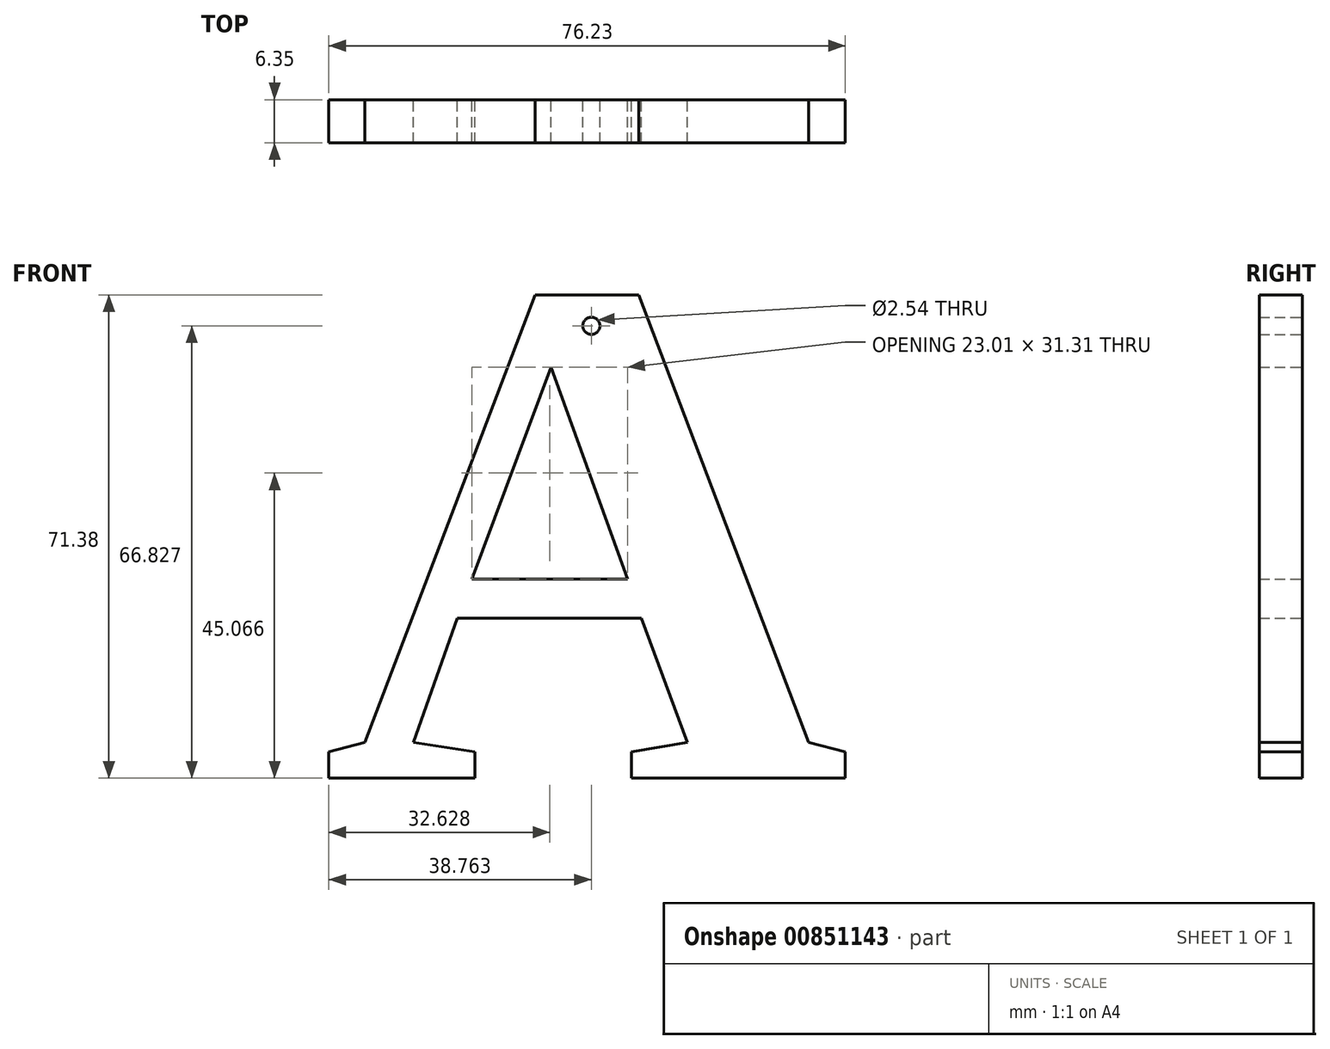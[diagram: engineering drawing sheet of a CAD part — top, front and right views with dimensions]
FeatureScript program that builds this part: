
annotation { "Feature Type Name" : "Feature", "Feature Type Description" : "" }
export const myFeature = defineFeature(function(context is Context, id is Id, definition is map)
    precondition{}
    {
        {
            var Q0;
            Q0=qCreatedBy(makeId("Front.planeOp"),FACE);
            var sketch = newSketch(context, id + "F0", { "sketchPlane" : qUnion([Q0])});
            skText(sketch, "E0", { "text": "A", "fontName": "Tinos-Bold.ttf"});
            const initialGuessF0  = {"E0": [-0.0566, -0.03993, 1, 0, 0.07785]};
            skSetInitialGuess(sketch, initialGuessF0);
            skSolve(sketch);
        }
        {
            var Q0;
            Q0=makeQuery(id+"F0.imprint","IMPRINT",FACE,{"disambiguationData":[TD([[makeQuery(id+"F0.imprint","IMPRINT",EDGE,{"derivedFrom":sQuery(id+"F0.wireOp",EDGE,"E0.sketch_text.stroke-0")}),-1.0]])]});
            var sketch = newSketch(context, id + "F1", { "sketchPlane" : qUnion([Q0])});
            skPoint(sketch, "E1", {"position": v(-16.78, 26.9) * mm});
            skSolve(sketch);
        }
        {
            var Q0;
            Q0=makeQuery(id+"F0.imprint","IMPRINT",FACE,{"disambiguationData":[TD([[makeQuery(id+"F0.imprint","IMPRINT",EDGE,{"derivedFrom":sQuery(id+"F0.wireOp",EDGE,"E0.sketch_text.stroke-0")}),-1.0]])]});
            extrude(context, id + "F2", {"entities" : qUnion([Q0]), "depth" : 6.35 * mm, "offsetDistance" : 25.4 * mm});
        }
        {
            var Q0;
            Q0=sQuery(id+"F1.wireOp",VERTEX,"E1");
            var Q1;
            Q1=makeQuery(id+"F2.opExtrude","SWEPT_BODY",BODY,{"disambiguationData":[OSD([sQuery(id+"F0.wireOp",EDGE,"E0.sketch_text.stroke-0"),sQuery(id+"F0.wireOp",EDGE,"E0.sketch_text.stroke-1"),sQuery(id+"F0.wireOp",EDGE,"E0.sketch_text.stroke-2"),sQuery(id+"F0.wireOp",EDGE,"E0.sketch_text.stroke-3"),sQuery(id+"F0.wireOp",EDGE,"E0.sketch_text.stroke-4"),sQuery(id+"F0.wireOp",EDGE,"E0.sketch_text.stroke-5"),sQuery(id+"F0.wireOp",EDGE,"E0.sketch_text.stroke-6"),sQuery(id+"F0.wireOp",EDGE,"E0.sketch_text.stroke-7"),sQuery(id+"F0.wireOp",EDGE,"E0.sketch_text.stroke-8"),sQuery(id+"F0.wireOp",EDGE,"E0.sketch_text.stroke-9"),sQuery(id+"F0.wireOp",EDGE,"E0.sketch_text.stroke-10"),sQuery(id+"F0.wireOp",EDGE,"E0.sketch_text.stroke-11"),sQuery(id+"F0.wireOp",EDGE,"E0.sketch_text.stroke-12"),sQuery(id+"F0.wireOp",EDGE,"E0.sketch_text.stroke-13"),sQuery(id+"F0.wireOp",EDGE,"E0.sketch_text.stroke-14"),sQuery(id+"F0.wireOp",EDGE,"E0.sketch_text.stroke-15"),sQuery(id+"F0.wireOp",EDGE,"E0.sketch_text.stroke-16"),sQuery(id+"F0.wireOp",EDGE,"E0.sketch_text.stroke-17"),sQuery(id+"F0.wireOp",EDGE,"E0.sketch_text.stroke-18")])]});
            hole(context, id + "F3", {"style" : HoleStyle.SIMPLE, "endStyle" : HoleEndStyle.THROUGH, "oppositeDirection" : true, "holeDiameter" : 2.54 * mm, "majorDiameter" : 6.35 * mm, "isTappedThrough" : true, "tappedDepth" : 12.7 * mm, "tapClearance" : 3, "locations" : qUnion([Q0]), "scope" : qUnion([Q1])});
        }
    });
